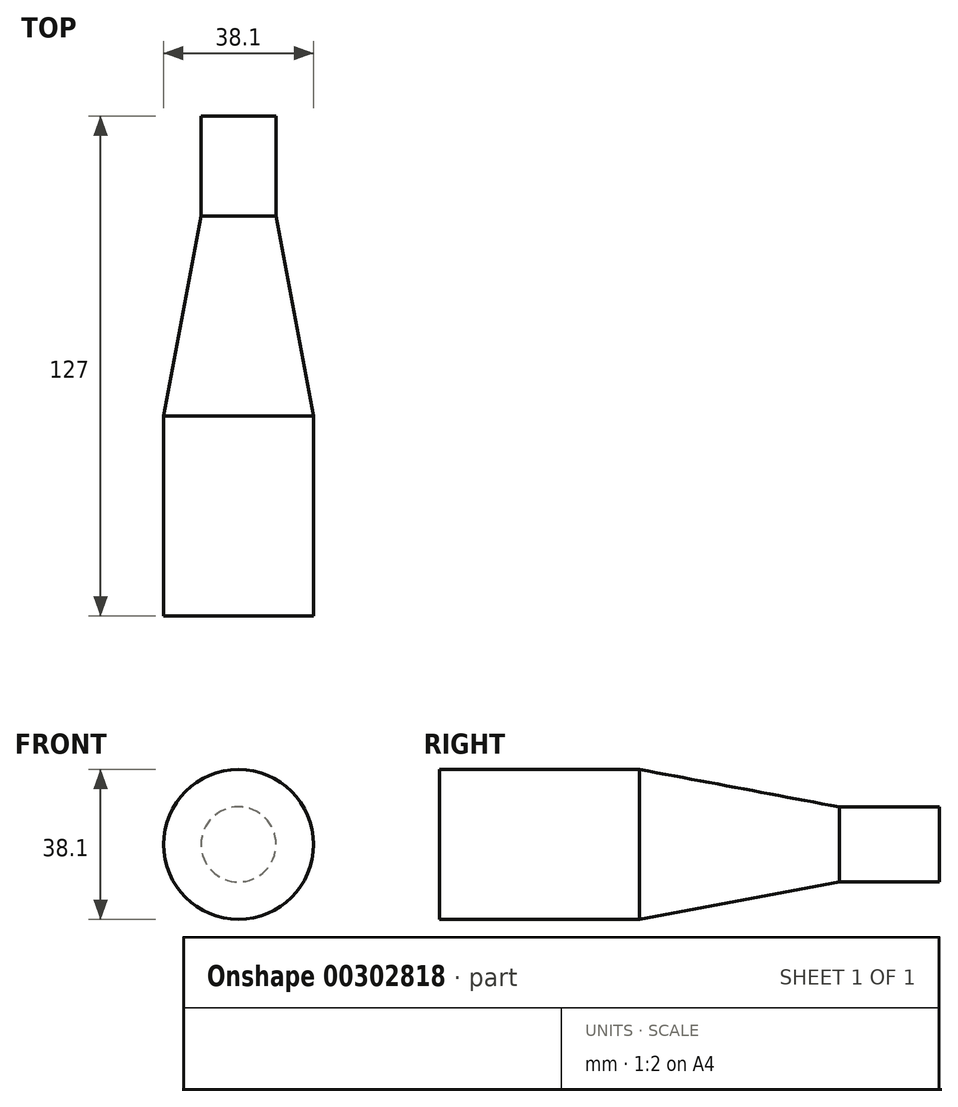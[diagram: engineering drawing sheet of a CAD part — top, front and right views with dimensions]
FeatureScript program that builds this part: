
annotation { "Feature Type Name" : "Feature", "Feature Type Description" : "" }
export const myFeature = defineFeature(function(context is Context, id is Id, definition is map)
    precondition{}
    {
        {
            var Q0;
            Q0=qCreatedBy(makeId("Right.planeOp"),FACE);
            var sketch = newSketch(context, id + "F0", { "sketchPlane" : qUnion([Q0])});
            skLineSegment(sketch, "E0", {"start": v(0, 0) * mm, "end": v(-127, 0) * mm});
            skLineSegment(sketch, "E1", {"start": v(-127, 0) * mm, "end": v(-127, 19.05) * mm});
            skLineSegment(sketch, "E2", {"start": v(-127, 19.05) * mm, "end": v(-76.2, 19.05) * mm});
            skLineSegment(sketch, "E3", {"start": v(-76.2, 19.05) * mm, "end": v(-25.4, 9.52) * mm});
            skLineSegment(sketch, "E4", {"start": v(-25.4, 9.52) * mm, "end": v(0, 9.53) * mm});
            skLineSegment(sketch, "E5", {"start": v(0, 9.53) * mm, "end": v(0, 0) * mm});
            skSolve(sketch);
        }
        {
            var Q0;
            Q0=makeQuery(id+"F0.imprint","IMPRINT",FACE,{"disambiguationData":[TD([[makeQuery(id+"F0.imprint","IMPRINT",EDGE,{"derivedFrom":sQuery(id+"F0.wireOp",EDGE,"E0")}),-1.0]])]});
            var Q1;
            Q1=sQuery(id+"F0.wireOp",EDGE,"E0");
            revolve(context, id + "F1", {"entities" : qUnion([Q0]), "axis" : qUnion([Q1]), "revolveType" : RevolveType.FULL});
        }
    });
